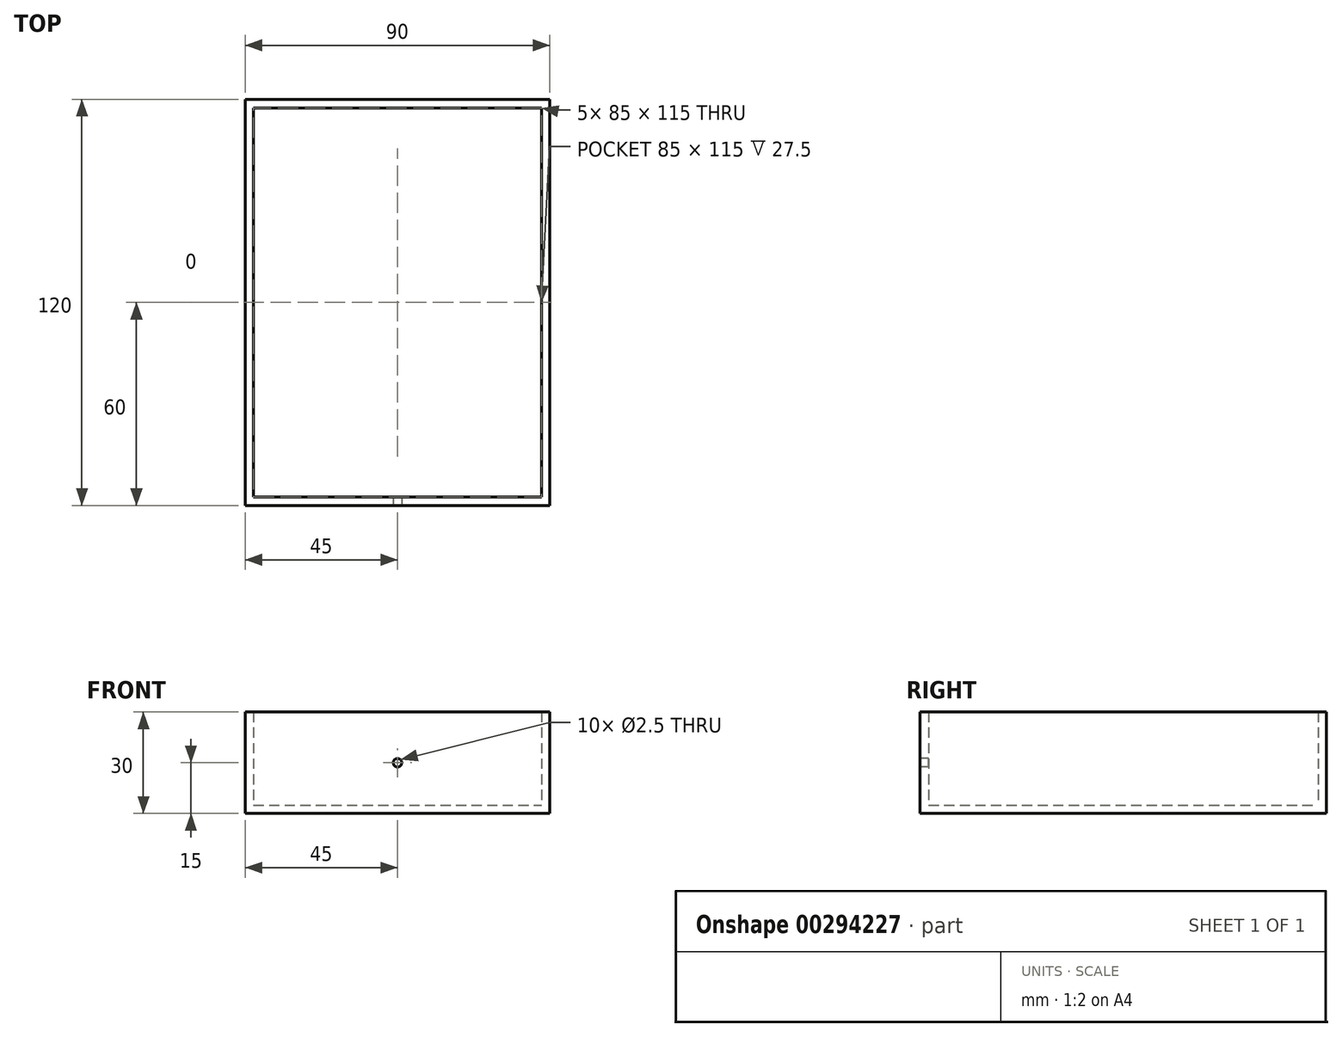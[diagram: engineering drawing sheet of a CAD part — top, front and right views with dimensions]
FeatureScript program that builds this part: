
annotation { "Feature Type Name" : "Feature", "Feature Type Description" : "" }
export const myFeature = defineFeature(function(context is Context, id is Id, definition is map)
    precondition{}
    {
        {
            var Q0;
            Q0=qCreatedBy(makeId("Front.planeOp"),FACE);
            var sketch = newSketch(context, id + "F0", { "sketchPlane" : qUnion([Q0])});
            skLineSegment(sketch, "E0.bottom", {"start": v(-45, 15) * mm, "end": v(45, 15) * mm});
            skLineSegment(sketch, "E0.top", {"start": v(-45, -15) * mm, "end": v(45, -15) * mm});
            skLineSegment(sketch, "E0.left", {"start": v(-45, 15) * mm, "end": v(-45, -15) * mm});
            skLineSegment(sketch, "E0.right", {"start": v(45, 15) * mm, "end": v(45, -15) * mm});
            skPoint(sketch, "E0.middle", {"position": v(0, 0) * mm});
            skSolve(sketch);
        }
        {
            var Q0;
            Q0 = qSketchRegion(id + "F0", true);
            extrude(context, id + "F1", {"entities" : qUnion([Q0]), "depth" : 120 * mm});
        }
        {
            var Q0;
            Q0=makeQuery(id+"F1.opExtrude","SWEPT_FACE",FACE,{"disambiguationData":[OSD([sQuery(id+"F0.wireOp",EDGE,"E0.bottom")])]});
            shell(context, id + "F2", {"entities" : qUnion([Q0]), "thickness" : 2.5 * mm});
        }
        {
            var Q0;
            Q0=makeQuery(id+"F1.opExtrude","CAP_FACE",FACE,{"disambiguationData":[OSD([sQuery(id+"F0.wireOp",EDGE,"E0.bottom"),sQuery(id+"F0.wireOp",EDGE,"E0.top"),sQuery(id+"F0.wireOp",EDGE,"E0.left"),sQuery(id+"F0.wireOp",EDGE,"E0.right")])],"isStart":false});
            var sketch = newSketch(context, id + "F3", { "sketchPlane" : qUnion([Q0])});
            skCircle(sketch, "E1", {"center": v(0, 0) * mm, "radius": 1.25 * mm});
            skSolve(sketch);
        }
        {
            var Q0;
            Q0 = qSketchRegion(id + "F3", true);
            extrude(context, id + "F4", {"entities" : qUnion([Q0]), "operationType" : NewBodyOperationType.REMOVE, "oppositeDirection" : true, "depth" : 25 * mm});
        }
    });
